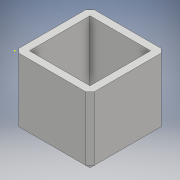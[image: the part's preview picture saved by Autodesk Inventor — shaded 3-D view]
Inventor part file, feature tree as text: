
AUTODESK INVENTOR PART (.ipt)
format: ipt  version: 2017 (Build 210142000, 142)  size: 117,760 bytes
history: native  units: mm
features: sketch x4, extrude x3, chamfer x1, thread x1
ambient origin geometry x8: Origin, YZ Plane, XZ Plane, XY Plane, X Axis, Y Axis, Z Axis, Center Point
bodies: Solid1 (feature_tree)
feature tree (9):
  extrude  "Extrusion1"  Depth=33.25mm
  sketch  "Sketch2"  dims[d2=30.0mm d3=0.0mm d4=26.75mm]
  extrude  "Extrusion2"  Depth=26.75mm
  chamfer  "Chamfer1"  Distance=26.75mm
  extrude  "Extrusion3"  Depth=10.0mm
  thread  "Thread1"  [1 undecoded]
  sketch  "Sketch1"  dims[d0=33.25mm d1=33.25mm]
  sketch  "Sketch3"  dims[d5=26.75mm d6=26.75mm d7=0.0mm]
  sketch  "Sketch4"  dims[d8=1.875mm d9=2.0mm d10=45.0deg d11=9.25mm d12=10.0mm d13=0.0mm d14=10.0mm d15=0.0mm]
note: 1 required parameter value undecoded (feature->parameter linkage not recoverable at this tier; creation-order binding heuristic only, values carry confidence <= 0.55)
